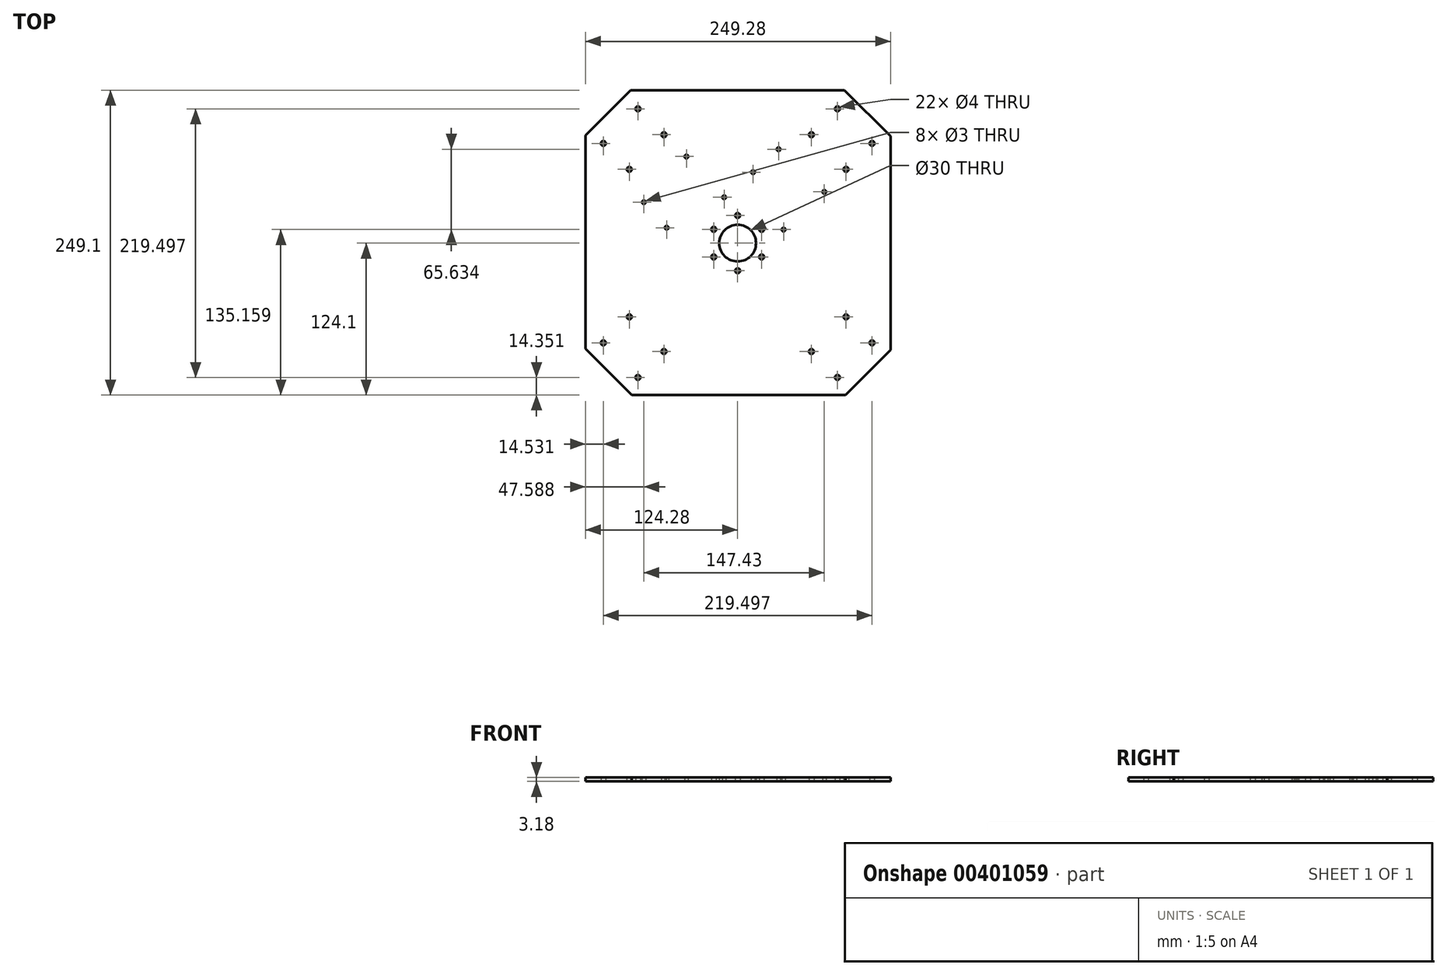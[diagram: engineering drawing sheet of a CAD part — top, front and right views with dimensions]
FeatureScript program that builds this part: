
annotation { "Feature Type Name" : "Feature", "Feature Type Description" : "" }
export const myFeature = defineFeature(function(context is Context, id is Id, definition is map)
    precondition{}
    {
        {
            var Q0;
            Q0=qCreatedBy(makeId("Top.planeOp"),FACE);
            var sketch = newSketch(context, id + "F0", { "sketchPlane" : qUnion([Q0])});
            skLineSegment(sketch, "E0.bottom", {"start": v(-87.43, 125) * mm, "end": v(87.24, 125) * mm});
            skLineSegment(sketch, "E0.top", {"start": v(-86.53, -124.1) * mm, "end": v(87.96, -124.1) * mm});
            skLineSegment(sketch, "E0.left", {"start": v(-124.28, 88.14) * mm, "end": v(-124.28, -86.34) * mm});
            skLineSegment(sketch, "E0.right", {"start": v(125, 87.24) * mm, "end": v(125, -87.24) * mm});
            skLineSegment(sketch, "E1", {"start": v(-124.28, -86.34) * mm, "end": v(-86.53, -124.1) * mm});
            skLineSegment(sketch, "E2", {"start": v(87.96, -124.1) * mm, "end": v(125, -87.24) * mm});
            skLineSegment(sketch, "E3", {"start": v(125, 87.24) * mm, "end": v(87.24, 125) * mm});
            skLineSegment(sketch, "E4", {"start": v(-87.43, 125) * mm, "end": v(-124.28, 88.14) * mm});
            skCircle(sketch, "E5", {"center": v(-109.75, 81.46) * mm, "radius": 2 * mm});
            skCircle(sketch, "E6", {"center": v(-81.46, 109.75) * mm, "radius": 2 * mm});
            skCircle(sketch, "E7", {"center": v(-88.54, 60.25) * mm, "radius": 2 * mm});
            skCircle(sketch, "E8", {"center": v(-60.25, 88.54) * mm, "radius": 2 * mm});
            skCircle(sketch, "E9.1.0", {"center": v(-81.46, -109.75) * mm, "radius": 2 * mm});
            skCircle(sketch, "E9.1.1", {"center": v(-109.75, -81.46) * mm, "radius": 2 * mm});
            skCircle(sketch, "E9.1.2", {"center": v(-88.54, -60.25) * mm, "radius": 2 * mm});
            skCircle(sketch, "E9.1.3", {"center": v(-60.25, -88.54) * mm, "radius": 2 * mm});
            skCircle(sketch, "E9.2.0", {"center": v(109.75, -81.46) * mm, "radius": 2 * mm});
            skCircle(sketch, "E9.2.1", {"center": v(81.46, -109.75) * mm, "radius": 2 * mm});
            skCircle(sketch, "E9.2.2", {"center": v(60.25, -88.54) * mm, "radius": 2 * mm});
            skCircle(sketch, "E9.2.3", {"center": v(88.54, -60.25) * mm, "radius": 2 * mm});
            skCircle(sketch, "E9.3.0", {"center": v(81.46, 109.75) * mm, "radius": 2 * mm});
            skCircle(sketch, "E9.3.1", {"center": v(109.75, 81.46) * mm, "radius": 2 * mm});
            skCircle(sketch, "E9.3.2", {"center": v(88.54, 60.25) * mm, "radius": 2 * mm});
            skCircle(sketch, "E9.3.3", {"center": v(60.25, 88.54) * mm, "radius": 2 * mm});
            skCircle(sketch, "E10", {"center": v(-76.7, 33.42) * mm, "radius": 1.5 * mm});
            skCircle(sketch, "E11", {"center": v(-11.06, 37.48) * mm, "radius": 1.5 * mm});
            skCircle(sketch, "E12", {"center": v(-57.98, 12.59) * mm, "radius": 1.5 * mm});
            skPoint(sketch, "E13.center", {"position": v(0, 0) * mm});
            skCircle(sketch, "E14", {"center": v(-41.88, 70.74) * mm, "radius": 1.5 * mm});
            skCircle(sketch, "E15.1.0", {"center": v(70.74, 41.88) * mm, "radius": 1.5 * mm});
            skCircle(sketch, "E15.1.1", {"center": v(33.42, 76.7) * mm, "radius": 1.5 * mm});
            skCircle(sketch, "E15.1.2", {"center": v(12.59, 57.98) * mm, "radius": 1.5 * mm});
            skCircle(sketch, "E15.1.3", {"center": v(37.48, 11.06) * mm, "radius": 1.5 * mm});
            skLineSegment(sketch, "E15.anchor1", {"start": v(0, 0) * mm, "end": v(-41.88, 70.74) * mm, "construction": true});
            skLineSegment(sketch, "E15.anchor2", {"start": v(0, 0) * mm, "end": v(70.74, 41.88) * mm, "construction": true});
            skCircle(sketch, "E16", {"center": v(0, 22.58) * mm, "radius": 2 * mm});
            skCircle(sketch, "E17.1.0", {"center": v(-19.56, 11.3) * mm, "radius": 2 * mm});
            skCircle(sketch, "E17.2.0", {"center": v(-19.56, -11.3) * mm, "radius": 2 * mm});
            skCircle(sketch, "E17.3.0", {"center": v(0, -22.58) * mm, "radius": 2 * mm});
            skCircle(sketch, "E17.4.0", {"center": v(19.56, -11.3) * mm, "radius": 2 * mm});
            skCircle(sketch, "E17.5.0", {"center": v(19.56, 11.3) * mm, "radius": 2 * mm});
            skCircle(sketch, "E18", {"center": v(0, 0) * mm, "radius": 15 * mm});
            skSolve(sketch);
        }
        {
            var Q0;
            Q0=makeQuery(id+"F0.imprint","IMPRINT",FACE,{"disambiguationData":[TD([[makeQuery(id+"F0.imprint","IMPRINT",EDGE,{"derivedFrom":sQuery(id+"F0.wireOp",EDGE,"E0.bottom")}),-1.0]])]});
            extrude(context, id + "F1", {"entities" : qUnion([Q0]), "depth" : 3.17 * mm});
        }
    });
